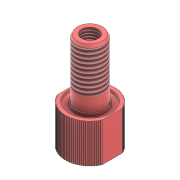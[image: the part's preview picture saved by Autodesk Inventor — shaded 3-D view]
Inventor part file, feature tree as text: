
AUTODESK INVENTOR PART (.ipt)
format: ipt  version: 2022.3 (Build 263350000, 350)  size: 541,696 bytes
history: native  units: mm
features: extrude x7, sketch x7, thread x3, chamfer x2, other x1
ambient origin geometry x8: Origin, YZ Plane, XZ Plane, XY Plane, X Axis, Y Axis, Z Axis, Center Point
bodies: Body1 (feature_tree)
feature tree (20):
  other  "Sólido1"
  extrude  "Extrusión1"  Depth=14.0mm
  extrude  "Extrusión2"  Depth=14.0mm TaperAngle=0.0deg
  extrude  "Extrusión3"  Depth=21.1mm TaperAngle=0.0deg
  thread  "Rosca1"  [1 undecoded]
  extrude  "Extrusión4"  Depth=21.1mm TaperAngle=0.0deg
  extrude  "Extrusión5"  Depth=12.0mm TaperAngle=0.0deg
  thread  "Rosca2"  [1 undecoded]
  extrude  "Extrusión6"  Depth=1.0mm TaperAngle=0.0deg
  thread  "Rosca3"  [1 undecoded]
  chamfer  "Chaflán1"  Distance=2.0mm Angle=45.0deg
  chamfer  "Chaflán2"  Distance=1.0mm Angle=45.0deg
  extrude  "Extrusión7"  Depth=1.0mm
  sketch  "Boceto1"  dims[d0=14.0mm d1=0.0mm d2=8.0mm]
  sketch  "Boceto2"  dims[d3=8.0mm d4=14.0mm d5=0.0mm]
  sketch  "Boceto3"  dims[d6=10.0mm d7=21.1mm d8=0.0mm d9=21.1mm d10=5.0mm]
  sketch  "Boceto4"  dims[d11=5.0mm d12=21.1mm d13=0.0mm]
  sketch  "Boceto5"  dims[d14=10.0mm d15=12.0mm d16=0.0mm d17=5.0mm d18=0.0mm]
  sketch  "Boceto6"  dims[d19=6.0mm d20=6.2mm d21=0.0mm d22=6.2mm d23=0.0mm d24=0.5mm d25=2.0mm d26=45.0deg d27=0.5mm d28=1.0mm d29=45.0deg]
  sketch  "Boceto7"  dims[d30=15.0mm d31=11.0mm d32=1.0mm d33=0.0mm]
note: 3 required parameter values undecoded (feature->parameter linkage not recoverable at this tier; creation-order binding heuristic only, values carry confidence <= 0.55)
